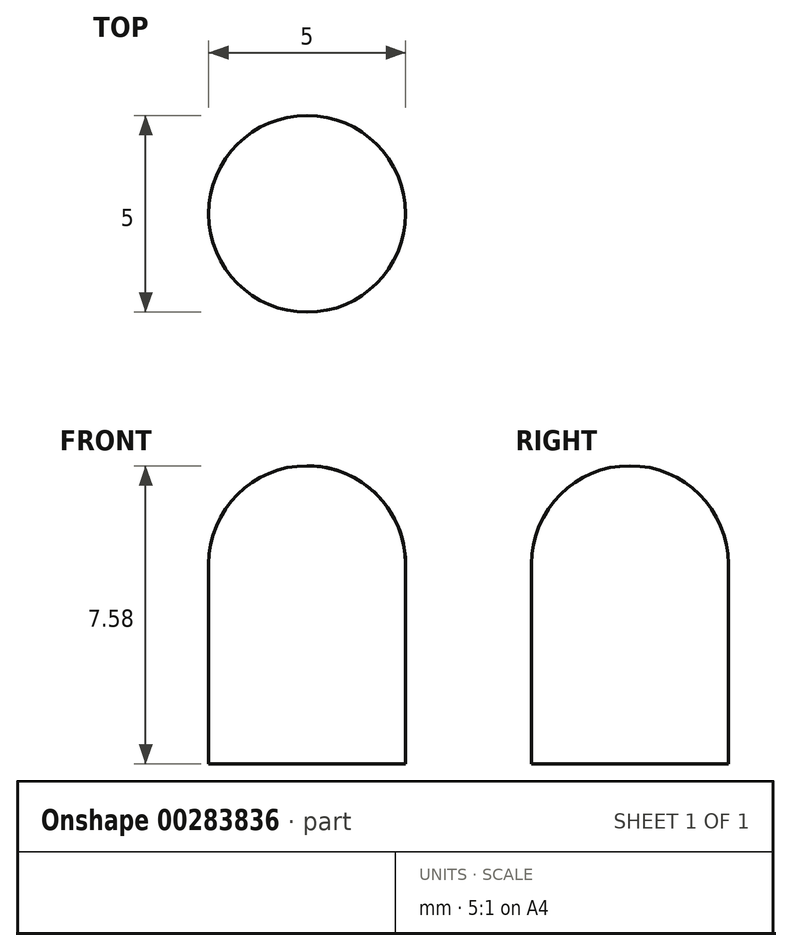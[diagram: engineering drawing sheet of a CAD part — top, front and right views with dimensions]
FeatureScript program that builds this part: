
annotation { "Feature Type Name" : "Feature", "Feature Type Description" : "" }
export const myFeature = defineFeature(function(context is Context, id is Id, definition is map)
    precondition{}
    {
        {
            var Q0;
            Q0=qCreatedBy(makeId("Front.planeOp"),FACE);
            var sketch = newSketch(context, id + "F0", { "sketchPlane" : qUnion([Q0])});
            skLineSegment(sketch, "E0", {"start": v(0, 0) * mm, "end": v(-2.5, 0) * mm});
            skLineSegment(sketch, "E1", {"start": v(-2.5, 0) * mm, "end": v(-2.5, 5.08) * mm});
            skArc(sketch, "E2", {"start": v(-2.5, 5.08) * mm, "mid": v(-1.77, 6.85) * mm, "end": v(0, 7.58) * mm});
            skLineSegment(sketch, "E3", {"start": v(0, 7.58) * mm, "end": v(0, 0) * mm});
            skSolve(sketch);
        }
        {
            var Q0;
            Q0=makeQuery(id+"F0.imprint","IMPRINT",FACE,{"disambiguationData":[TD([[makeQuery(id+"F0.imprint","IMPRINT",EDGE,{"derivedFrom":sQuery(id+"F0.wireOp",EDGE,"E0")}),-1.0]])]});
            var Q1;
            Q1=sQuery(id+"F0.wireOp",EDGE,"E3");
            revolve(context, id + "F1", {"entities" : qUnion([Q0]), "axis" : qUnion([Q1]), "revolveType" : RevolveType.FULL});
        }
    });
